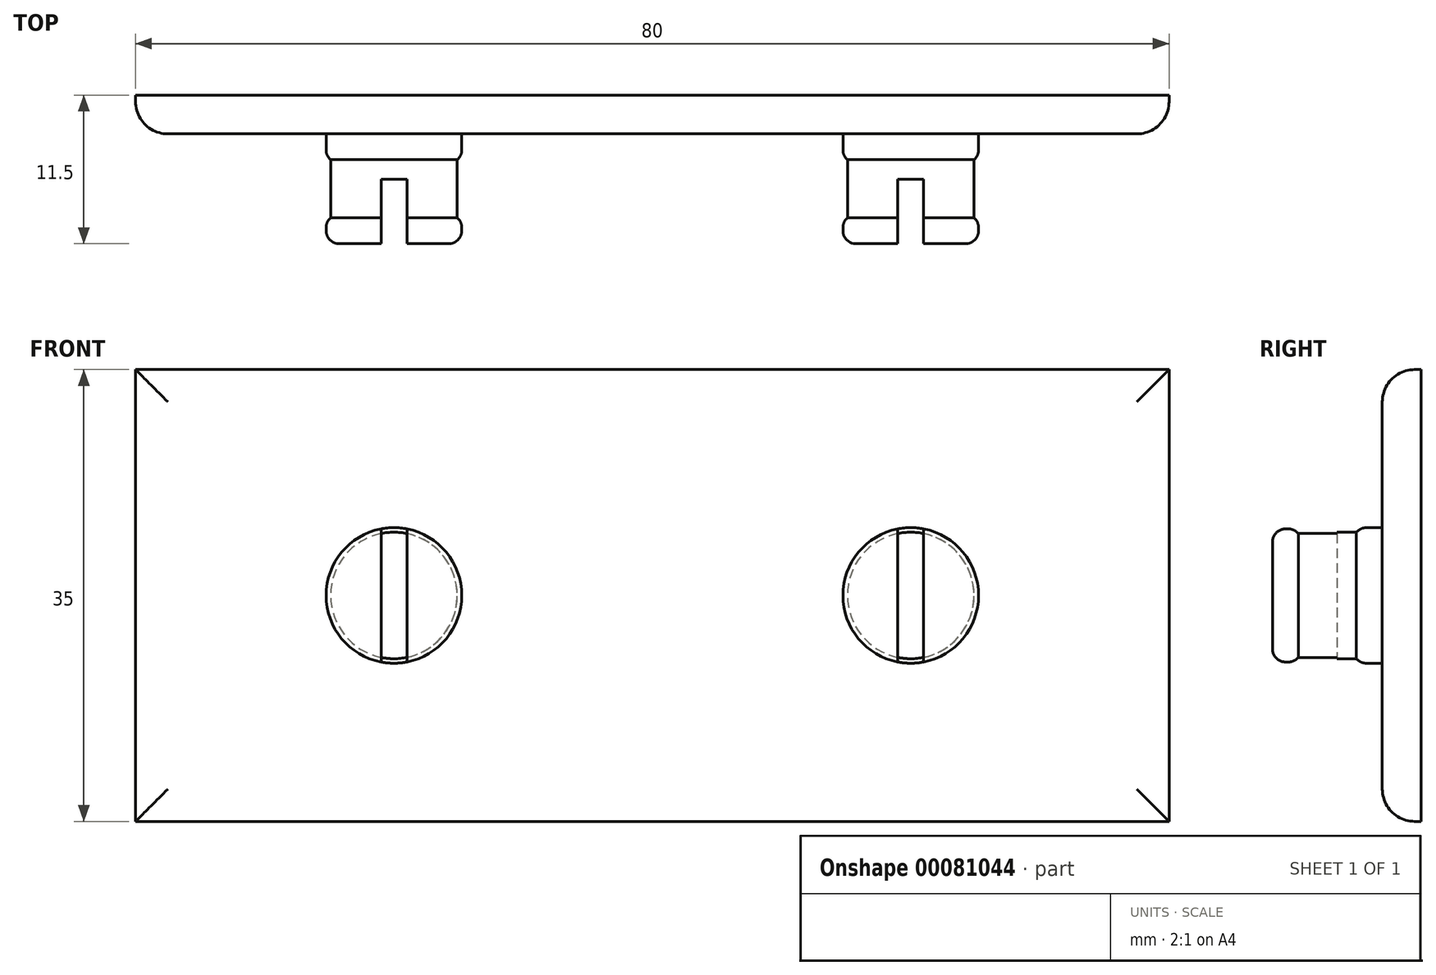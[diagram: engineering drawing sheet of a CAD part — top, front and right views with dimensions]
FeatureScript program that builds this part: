
annotation { "Feature Type Name" : "Feature", "Feature Type Description" : "" }
export const myFeature = defineFeature(function(context is Context, id is Id, definition is map)
    precondition{}
    {
        {
            var Q0;
            Q0=qCreatedBy(makeId("Front.planeOp"),FACE);
            var sketch = newSketch(context, id + "F0", { "sketchPlane" : qUnion([Q0])});
            skLineSegment(sketch, "E0.bottom", {"start": v(40, -17.5) * mm, "end": v(-40, -17.5) * mm});
            skLineSegment(sketch, "E0.top", {"start": v(40, 17.5) * mm, "end": v(-40, 17.5) * mm});
            skLineSegment(sketch, "E0.left", {"start": v(40, -17.5) * mm, "end": v(40, 17.5) * mm});
            skLineSegment(sketch, "E0.right", {"start": v(-40, -17.5) * mm, "end": v(-40, 17.5) * mm});
            skPoint(sketch, "E0.middle", {"position": v(0, 0) * mm});
            skSolve(sketch);
        }
        {
            var Q0;
            Q0=makeQuery(id+"F0.imprint","IMPRINT",FACE,{"disambiguationData":[TD([[makeQuery(id+"F0.imprint","IMPRINT",EDGE,{"derivedFrom":sQuery(id+"F0.wireOp",EDGE,"E0.bottom")}),-1.0]])]});
            extrude(context, id + "F1", {"entities" : qUnion([Q0]), "depth" : 3 * mm});
        }
        {
            var Q0;
            Q0=makeQuery(id+"F1.opExtrude","CAP_FACE",FACE,{"disambiguationData":[OSD([sQuery(id+"F0.wireOp",EDGE,"E0.bottom"),sQuery(id+"F0.wireOp",EDGE,"E0.top"),sQuery(id+"F0.wireOp",EDGE,"E0.left"),sQuery(id+"F0.wireOp",EDGE,"E0.right")])],"isStart":false});
            var sketch = newSketch(context, id + "F2", { "sketchPlane" : qUnion([Q0])});
            skLineSegment(sketch, "E1", {"start": v(0, 0) * mm, "end": v(0, 451.8) * mm, "construction": true});
            skCircle(sketch, "E2", {"center": v(-20, 0) * mm, "radius": 5.25 * mm});
            skCircle(sketch, "E3.MirrorC", {"center": v(20, 0) * mm, "radius": 5.25 * mm});
            skSolve(sketch);
        }
        {
            var Q0;
            Q0 = qSketchRegion(id + "F2", true);
            extrude(context, id + "F3", {"entities" : qUnion([Q0]), "operationType" : NewBodyOperationType.ADD, "depth" : 2 * mm});
        }
        {
            var Q0;
            Q0=makeQuery(id+"F3.opExtrude","CAP_FACE",FACE,{"disambiguationData":[OSD([sQuery(id+"F2.wireOp",EDGE,"E2")])],"isStart":false});
            var sketch = newSketch(context, id + "F4", { "sketchPlane" : qUnion([Q0])});
            skLineSegment(sketch, "E4", {"start": v(0, 0) * mm, "end": v(0, 13.5) * mm, "construction": true});
            skCircle(sketch, "E5", {"center": v(-20, 0) * mm, "radius": 4.9 * mm});
            skCircle(sketch, "E6.MirrorC", {"center": v(20, 0) * mm, "radius": 4.9 * mm});
            skSolve(sketch);
        }
        {
            var Q0;
            Q0 = qSketchRegion(id + "F4", true);
            extrude(context, id + "F5", {"entities" : qUnion([Q0]), "operationType" : NewBodyOperationType.ADD, "depth" : 4.5 * mm});
        }
        {
            var Q0;
            Q0=makeQuery(id+"F5.opExtrude","CAP_FACE",FACE,{"disambiguationData":[OSD([sQuery(id+"F4.wireOp",EDGE,"E5")])],"isStart":false});
            var sketch = newSketch(context, id + "F6", { "sketchPlane" : qUnion([Q0])});
            skLineSegment(sketch, "E7", {"start": v(0, 0) * mm, "end": v(0, 11.92) * mm, "construction": true});
            skCircle(sketch, "E8", {"center": v(-20, 0) * mm, "radius": 5.25 * mm});
            skCircle(sketch, "E9.MirrorC", {"center": v(20, 0) * mm, "radius": 5.25 * mm});
            skSolve(sketch);
        }
        {
            var Q0;
            Q0 = qSketchRegion(id + "F6", true);
            extrude(context, id + "F7", {"entities" : qUnion([Q0]), "operationType" : NewBodyOperationType.ADD, "depth" : 2 * mm});
        }
        {
            var Q0;
            Q0=makeQuery(id+"F3.opExtrude","CAP_EDGE",EDGE,{"disambiguationData":[OSD([sQuery(id+"F2.wireOp",EDGE,"E2")])],"isStart":true});
            var Q1;
            Q1=makeQuery(id+"F3.opExtrude","CAP_EDGE",EDGE,{"disambiguationData":[OSD([sQuery(id+"F2.wireOp",EDGE,"E2")])],"isStart":false});
            var Q2;
            Q2=makeQuery(id+"F7.opExtrude","CAP_EDGE",EDGE,{"disambiguationData":[OSD([sQuery(id+"F6.wireOp",EDGE,"E8")])],"isStart":true});
            var Q3;
            Q3=makeQuery(id+"F7.opExtrude","CAP_EDGE",EDGE,{"disambiguationData":[OSD([sQuery(id+"F6.wireOp",EDGE,"E8")])],"isStart":false});
            var Q4;
            Q4=makeQuery(id+"F3.opExtrude","CAP_EDGE",EDGE,{"disambiguationData":[OSD([sQuery(id+"F2.wireOp",EDGE,"E3.MirrorC")])],"isStart":true});
            var Q5;
            Q5=makeQuery(id+"F3.opExtrude","CAP_EDGE",EDGE,{"disambiguationData":[OSD([sQuery(id+"F2.wireOp",EDGE,"E3.MirrorC")])],"isStart":false});
            var Q6;
            Q6=makeQuery(id+"F7.opExtrude","CAP_EDGE",EDGE,{"disambiguationData":[OSD([sQuery(id+"F6.wireOp",EDGE,"E9.MirrorC")])],"isStart":true});
            var Q7;
            Q7=makeQuery(id+"F7.opExtrude","CAP_EDGE",EDGE,{"disambiguationData":[OSD([sQuery(id+"F6.wireOp",EDGE,"E9.MirrorC")])],"isStart":false});
            fillet(context, id + "F8", {"entities" : qUnion([Q0, Q1, Q2, Q3, Q4, Q5, Q6, Q7]), "radius" : 1 * mm, "tangentPropagation" : true, "allowEdgeOverflow" : false});
        }
        {
            var Q0;
            Q0=makeQuery(id+"F7.opExtrude","CAP_FACE",FACE,{"disambiguationData":[OSD([sQuery(id+"F6.wireOp",EDGE,"E8")])],"isStart":false});
            var sketch = newSketch(context, id + "F9", { "sketchPlane" : qUnion([Q0])});
            skLineSegment(sketch, "E10", {"start": v(0, 0) * mm, "end": v(0, 10.36) * mm, "construction": true});
            skLineSegment(sketch, "E11.bottom", {"start": v(-21, 7.5) * mm, "end": v(-19, 7.5) * mm});
            skLineSegment(sketch, "E11.top", {"start": v(-21, -7.5) * mm, "end": v(-19, -7.5) * mm});
            skLineSegment(sketch, "E11.left", {"start": v(-21, 7.5) * mm, "end": v(-21, -7.5) * mm});
            skLineSegment(sketch, "E11.right", {"start": v(-19, 7.5) * mm, "end": v(-19, -7.5) * mm});
            skPoint(sketch, "E11.middle", {"position": v(-20, 0) * mm});
            skLineSegment(sketch, "E12.MirrorCS", {"start": v(19, 7.5) * mm, "end": v(19, -7.5) * mm});
            skLineSegment(sketch, "E13.MirrorCS", {"start": v(21, 7.5) * mm, "end": v(19, 7.5) * mm});
            skLineSegment(sketch, "E14.MirrorCS", {"start": v(21, 7.5) * mm, "end": v(21, -7.5) * mm});
            skLineSegment(sketch, "E15.MirrorCS", {"start": v(21, -7.5) * mm, "end": v(19, -7.5) * mm});
            skSolve(sketch);
        }
        {
            var Q0;
            Q0 = qSketchRegion(id + "F9", true);
            extrude(context, id + "F10", {"entities" : qUnion([Q0]), "operationType" : NewBodyOperationType.REMOVE, "oppositeDirection" : true, "depth" : 5 * mm});
        }
        {
            var Q0;
            Q0=makeQuery(id+"F1.opExtrude","CAP_EDGE",EDGE,{"disambiguationData":[OSD([sQuery(id+"F0.wireOp",EDGE,"E0.right")])],"isStart":false});
            var Q1;
            Q1=makeQuery(id+"F1.opExtrude","CAP_EDGE",EDGE,{"disambiguationData":[OSD([sQuery(id+"F0.wireOp",EDGE,"E0.top")])],"isStart":false});
            var Q2;
            Q2=makeQuery(id+"F1.opExtrude","CAP_EDGE",EDGE,{"disambiguationData":[OSD([sQuery(id+"F0.wireOp",EDGE,"E0.left")])],"isStart":false});
            var Q3;
            Q3=makeQuery(id+"F1.opExtrude","CAP_EDGE",EDGE,{"disambiguationData":[OSD([sQuery(id+"F0.wireOp",EDGE,"E0.bottom")])],"isStart":false});
            fillet(context, id + "F11", {"entities" : qUnion([Q0, Q1, Q2, Q3]), "radius" : 2.5 * mm, "tangentPropagation" : true, "allowEdgeOverflow" : false});
        }
    });
